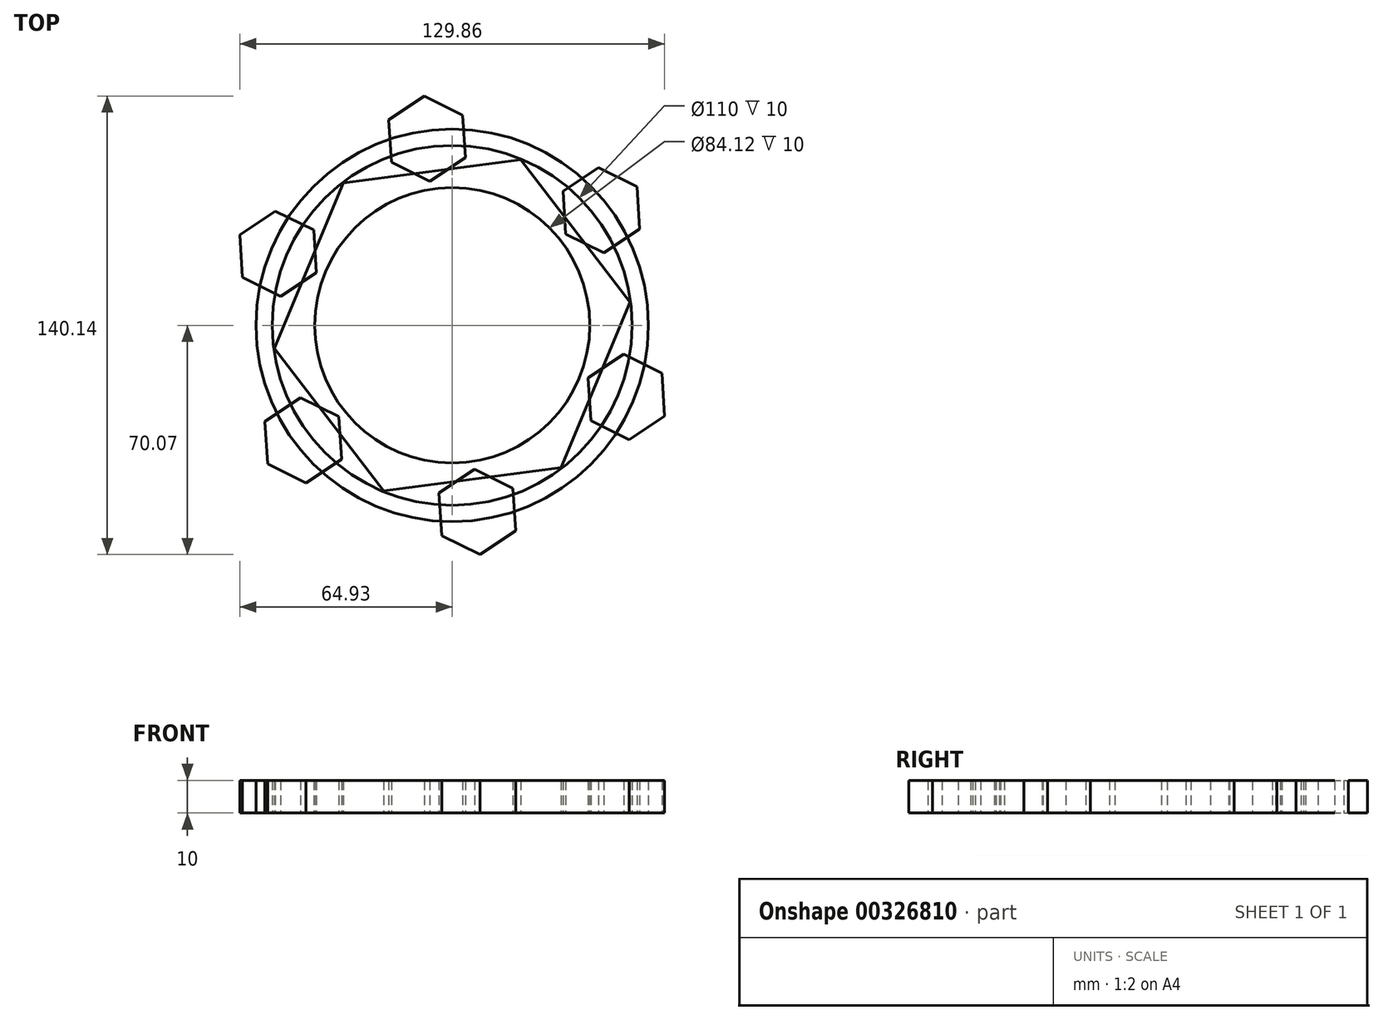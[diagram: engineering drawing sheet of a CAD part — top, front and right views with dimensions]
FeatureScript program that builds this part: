
annotation { "Feature Type Name" : "Feature", "Feature Type Description" : "" }
export const myFeature = defineFeature(function(context is Context, id is Id, definition is map)
    precondition{}
    {
        {
            var Q0;
            Q0=qCreatedBy(makeId("Top.planeOp"),FACE);
            var sketch = newSketch(context, id + "F0", { "sketchPlane" : qUnion([Q0])});
            skCircle(sketch, "E0", {"center": v(0, 0) * mm, "radius": 60 * mm});
            skSolve(sketch);
        }
        {
            var Q0;
            Q0=makeQuery(id+"F0.imprint","IMPRINT",FACE,{"disambiguationData":[TD([[makeQuery(id+"F0.imprint","IMPRINT",EDGE,{"derivedFrom":sQuery(id+"F0.wireOp",EDGE,"E0")}),1.0]])]});
            extrude(context, id + "F1", {"entities" : qUnion([Q0]), "depth" : 10 * mm});
        }
        {
            var Q0;
            Q0=qCreatedBy(makeId("Top.planeOp"),FACE);
            var sketch = newSketch(context, id + "F2", { "sketchPlane" : qUnion([Q0])});
            skCircle(sketch, "E1", {"center": v(0, 0) * mm, "radius": 55 * mm});
            skSolve(sketch);
        }
        {
            var Q0;
            Q0=makeQuery(id+"F2.imprint","IMPRINT",FACE,{"disambiguationData":[TD([[makeQuery(id+"F2.imprint","IMPRINT",EDGE,{"derivedFrom":sQuery(id+"F2.wireOp",EDGE,"E1")}),1.0]])]});
            extrude(context, id + "F3", {"entities" : qUnion([Q0]), "operationType" : NewBodyOperationType.REMOVE, "depth" : 10 * mm});
        }
        {
            var Q0;
            Q0=qCreatedBy(makeId("Top.planeOp"),FACE);
            var sketch = newSketch(context, id + "F4", { "sketchPlane" : qUnion([Q0])});
            skCircle(sketch, "E2.cCircle", {"center": v(0, 0) * mm, "radius": 47.43 * mm, "construction": true});
            skLineSegment(sketch, "E2.0", {"start": v(21, 50.58) * mm, "end": v(54.3, 7.1) * mm});
            skLineSegment(sketch, "E2.1", {"start": v(54.3, 7.1) * mm, "end": v(33.3, -43.48) * mm});
            skLineSegment(sketch, "E2.2", {"start": v(33.3, -43.48) * mm, "end": v(-21, -50.58) * mm});
            skLineSegment(sketch, "E2.3", {"start": v(-21, -50.58) * mm, "end": v(-54.3, -7.1) * mm});
            skLineSegment(sketch, "E2.4", {"start": v(-54.3, -7.1) * mm, "end": v(-33.3, 43.48) * mm});
            skLineSegment(sketch, "E2.5", {"start": v(-33.3, 43.48) * mm, "end": v(21, 50.58) * mm});
            skPoint(sketch, "E2.0.midPoint", {"position": v(37.66, 28.84) * mm});
            skSolve(sketch);
        }
        {
            var Q0;
            Q0=makeQuery(id+"F4.imprint","IMPRINT",FACE,{"disambiguationData":[TD([[makeQuery(id+"F4.imprint","IMPRINT",EDGE,{"derivedFrom":sQuery(id+"F4.wireOp",EDGE,"E2.0")}),-1.0]])]});
            extrude(context, id + "F5", {"entities" : qUnion([Q0]), "depth" : 10 * mm});
        }
        {
            var Q0;
            Q0=qCreatedBy(makeId("Top.planeOp"),FACE);
            var sketch = newSketch(context, id + "F6", { "sketchPlane" : qUnion([Q0])});
            skCircle(sketch, "E3", {"center": v(0, 0) * mm, "radius": 42.06 * mm});
            skSolve(sketch);
        }
        {
            var Q0;
            Q0=makeQuery(id+"F6.imprint","IMPRINT",FACE,{"disambiguationData":[TD([[makeQuery(id+"F6.imprint","IMPRINT",EDGE,{"derivedFrom":sQuery(id+"F6.wireOp",EDGE,"E3")}),1.0]])]});
            extrude(context, id + "F7", {"entities" : qUnion([Q0]), "operationType" : NewBodyOperationType.REMOVE, "depth" : 10 * mm});
        }
        {
            var Q0;
            Q0=qCreatedBy(makeId("Top.planeOp"),FACE);
            var sketch = newSketch(context, id + "F8", { "sketchPlane" : qUnion([Q0])});
            skArc(sketch, "E4", {"start": v(-46.77, 37.59) * mm, "mid": v(-68.94, 28.33) * mm, "end": v(-59.68, 6.16) * mm});
            skArc(sketch, "E5.1.0", {"start": v(-55.94, -21.7) * mm, "mid": v(-59, -45.54) * mm, "end": v(-35.18, -48.6) * mm});
            skArc(sketch, "E5.2.0", {"start": v(-9.17, -59.3) * mm, "mid": v(9.93, -73.87) * mm, "end": v(24.5, -54.77) * mm});
            skArc(sketch, "E5.3.0", {"start": v(46.77, -37.59) * mm, "mid": v(68.94, -28.33) * mm, "end": v(59.68, -6.16) * mm});
            skArc(sketch, "E5.4.0", {"start": v(55.94, 21.7) * mm, "mid": v(59, 45.54) * mm, "end": v(35.18, 48.6) * mm});
            skArc(sketch, "E5.5.0", {"start": v(9.17, 59.3) * mm, "mid": v(-9.93, 73.87) * mm, "end": v(-24.5, 54.77) * mm});
            skPoint(sketch, "E5.center", {"position": v(0, 0) * mm});
            skCircle(sketch, "E6.cCircle", {"center": v(-53.23, 21.87) * mm, "radius": 13.07 * mm, "construction": true});
            skLineSegment(sketch, "E6.0", {"start": v(-64.93, 27.68) * mm, "end": v(-54.05, 34.91) * mm});
            skLineSegment(sketch, "E6.1", {"start": v(-54.05, 34.91) * mm, "end": v(-42.34, 29.1) * mm});
            skLineSegment(sketch, "E6.2", {"start": v(-42.34, 29.1) * mm, "end": v(-41.52, 16.06) * mm});
            skLineSegment(sketch, "E6.3", {"start": v(-41.52, 16.06) * mm, "end": v(-52.4, 8.83) * mm});
            skLineSegment(sketch, "E6.4", {"start": v(-52.4, 8.83) * mm, "end": v(-64.1, 14.64) * mm});
            skLineSegment(sketch, "E6.5", {"start": v(-64.1, 14.64) * mm, "end": v(-64.93, 27.68) * mm});
            skLineSegment(sketch, "E7.1.0", {"start": v(-56.44, -42.4) * mm, "end": v(-57.26, -29.35) * mm});
            skLineSegment(sketch, "E7.1.1", {"start": v(-57.26, -29.35) * mm, "end": v(-46.38, -22.12) * mm});
            skLineSegment(sketch, "E7.1.2", {"start": v(-46.38, -22.12) * mm, "end": v(-34.67, -27.93) * mm});
            skLineSegment(sketch, "E7.1.3", {"start": v(-34.67, -27.93) * mm, "end": v(-33.85, -40.97) * mm});
            skLineSegment(sketch, "E7.1.4", {"start": v(-33.85, -40.97) * mm, "end": v(-44.73, -48.2) * mm});
            skLineSegment(sketch, "E7.1.5", {"start": v(-44.73, -48.2) * mm, "end": v(-56.44, -42.4) * mm});
            skLineSegment(sketch, "E7.2.0", {"start": v(8.5, -70.07) * mm, "end": v(-3.21, -64.26) * mm});
            skLineSegment(sketch, "E7.2.1", {"start": v(-3.21, -64.26) * mm, "end": v(-4.04, -51.22) * mm});
            skLineSegment(sketch, "E7.2.2", {"start": v(-4.04, -51.22) * mm, "end": v(6.85, -43.99) * mm});
            skLineSegment(sketch, "E7.2.3", {"start": v(6.85, -43.99) * mm, "end": v(18.55, -49.8) * mm});
            skLineSegment(sketch, "E7.2.4", {"start": v(18.55, -49.8) * mm, "end": v(19.37, -62.84) * mm});
            skLineSegment(sketch, "E7.2.5", {"start": v(19.37, -62.84) * mm, "end": v(8.5, -70.07) * mm});
            skLineSegment(sketch, "E7.3.0", {"start": v(64.93, -27.68) * mm, "end": v(54.05, -34.91) * mm});
            skLineSegment(sketch, "E7.3.1", {"start": v(54.05, -34.91) * mm, "end": v(42.34, -29.1) * mm});
            skLineSegment(sketch, "E7.3.2", {"start": v(42.34, -29.1) * mm, "end": v(41.52, -16.06) * mm});
            skLineSegment(sketch, "E7.3.3", {"start": v(41.52, -16.06) * mm, "end": v(52.4, -8.83) * mm});
            skLineSegment(sketch, "E7.3.4", {"start": v(52.4, -8.83) * mm, "end": v(64.1, -14.64) * mm});
            skLineSegment(sketch, "E7.3.5", {"start": v(64.1, -14.64) * mm, "end": v(64.93, -27.68) * mm});
            skLineSegment(sketch, "E7.4.0", {"start": v(56.44, 42.4) * mm, "end": v(57.26, 29.35) * mm});
            skLineSegment(sketch, "E7.4.1", {"start": v(57.26, 29.35) * mm, "end": v(46.38, 22.12) * mm});
            skLineSegment(sketch, "E7.4.2", {"start": v(46.38, 22.12) * mm, "end": v(34.67, 27.93) * mm});
            skLineSegment(sketch, "E7.4.3", {"start": v(34.67, 27.93) * mm, "end": v(33.85, 40.97) * mm});
            skLineSegment(sketch, "E7.4.4", {"start": v(33.85, 40.97) * mm, "end": v(44.73, 48.2) * mm});
            skLineSegment(sketch, "E7.4.5", {"start": v(44.73, 48.2) * mm, "end": v(56.44, 42.4) * mm});
            skLineSegment(sketch, "E7.5.0", {"start": v(-8.5, 70.07) * mm, "end": v(3.21, 64.26) * mm});
            skLineSegment(sketch, "E7.5.1", {"start": v(3.21, 64.26) * mm, "end": v(4.04, 51.22) * mm});
            skLineSegment(sketch, "E7.5.2", {"start": v(4.04, 51.22) * mm, "end": v(-6.85, 43.99) * mm});
            skLineSegment(sketch, "E7.5.3", {"start": v(-6.85, 43.99) * mm, "end": v(-18.55, 49.8) * mm});
            skLineSegment(sketch, "E7.5.4", {"start": v(-18.55, 49.8) * mm, "end": v(-19.37, 62.84) * mm});
            skLineSegment(sketch, "E7.5.5", {"start": v(-19.37, 62.84) * mm, "end": v(-8.5, 70.07) * mm});
            skSolve(sketch);
        }
        {
            var Q0;
            Q0 = qSketchRegion(id + "F8", true);
            extrude(context, id + "F9", {"entities" : qUnion([Q0]), "depth" : 10 * mm});
        }
    });
